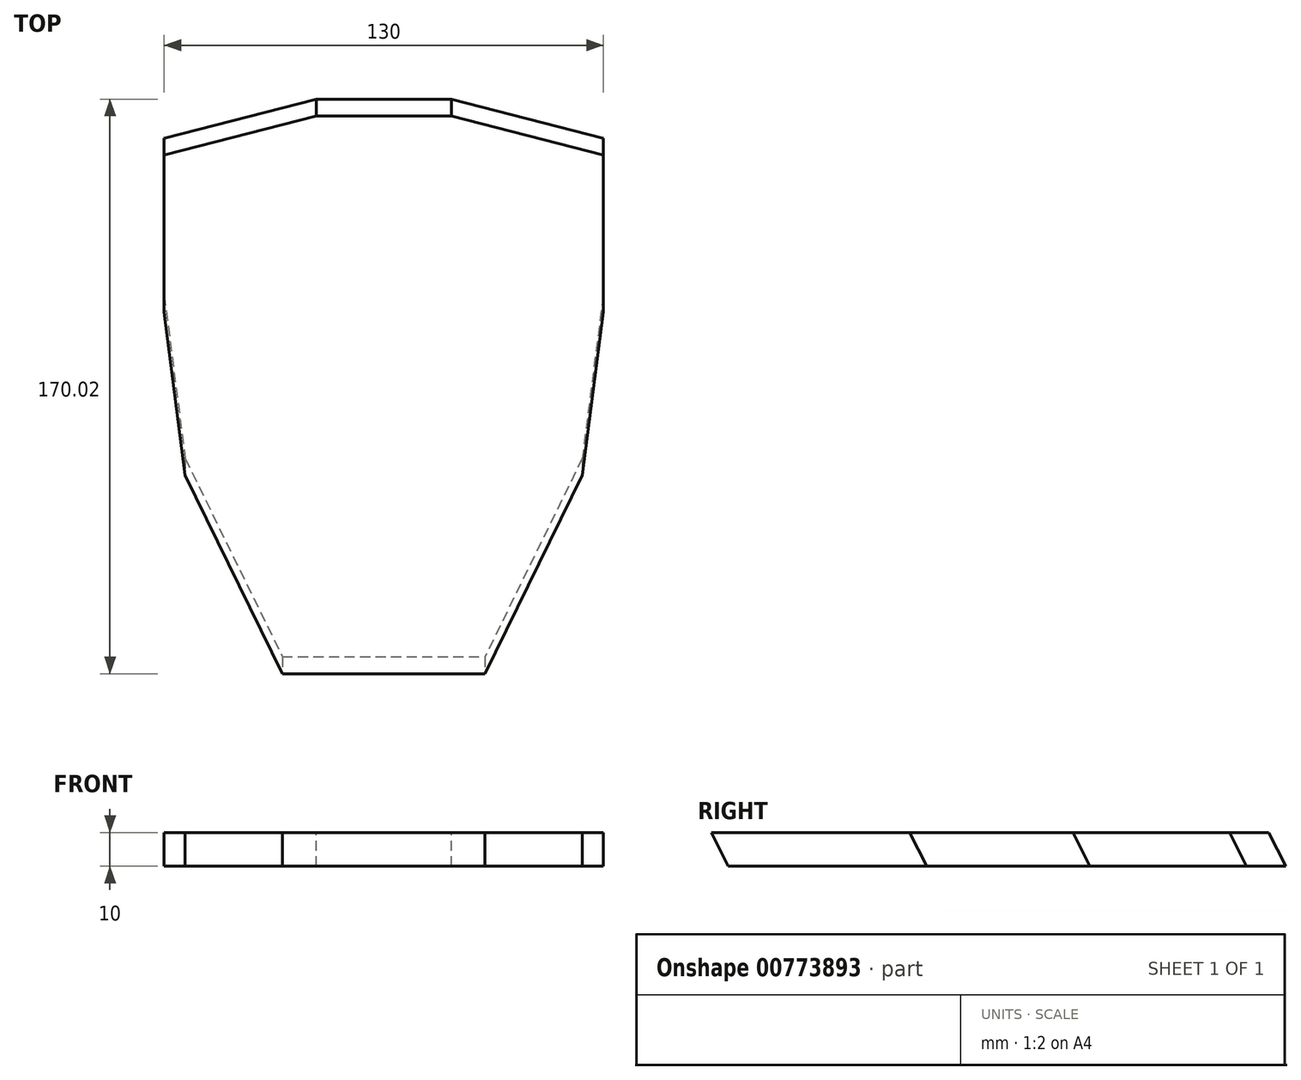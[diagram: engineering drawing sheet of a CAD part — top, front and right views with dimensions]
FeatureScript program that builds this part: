
annotation { "Feature Type Name" : "Feature", "Feature Type Description" : "" }
export const myFeature = defineFeature(function(context is Context, id is Id, definition is map)
    precondition{}
    {
        {
            var Q0;
            Q0=qCreatedBy(makeId("Top.planeOp"),FACE);
            var sketch = newSketch(context, id + "F0", { "sketchPlane" : qUnion([Q0])});
            skLineSegment(sketch, "E0", {"start": v(20, 40.27) * mm, "end": v(-20, 40.27) * mm});
            skPoint(sketch, "E1.orphan", {"position": v(0, 40.27) * mm});
            skLineSegment(sketch, "E2", {"start": v(-20, 40.27) * mm, "end": v(-65, 28.68) * mm});
            skLineSegment(sketch, "E3.MirrorCS", {"start": v(20, 40.27) * mm, "end": v(65, 28.68) * mm});
            skLineSegment(sketch, "E4", {"start": v(-65, 28.68) * mm, "end": v(-65, -17.7) * mm});
            skLineSegment(sketch, "E5", {"start": v(-65, -17.7) * mm, "end": v(-58.77, -66.04) * mm});
            skLineSegment(sketch, "E6", {"start": v(-58.77, -66.04) * mm, "end": v(-30, -124.75) * mm});
            skLineSegment(sketch, "E7", {"start": v(-30, -124.75) * mm, "end": v(30, -124.75) * mm});
            skLineSegment(sketch, "E8.MirrorCS", {"start": v(58.77, -66.04) * mm, "end": v(30, -124.75) * mm});
            skLineSegment(sketch, "E9.MirrorCS", {"start": v(65, -17.7) * mm, "end": v(58.77, -66.04) * mm});
            skLineSegment(sketch, "E10.MirrorCS", {"start": v(65, 28.68) * mm, "end": v(65, -17.7) * mm});
            skSolve(sketch);
        }
        {
            var Q0;
            Q0=qCreatedBy(makeId("Top.planeOp"),FACE);
            cPlane(context, id + "F1", {"entities" : qUnion([Q0]), "cplaneType" : CPlaneType.OFFSET, "offset" : 10 * mm, "width" : 150 * mm, "height" : 150 * mm});
        }
        {
            var Q0;
            Q0=qCreatedBy(id+"F1.planeOp",FACE);
            var sketch = newSketch(context, id + "F2", { "sketchPlane" : qUnion([Q0])});
            skLineSegment(sketch, "E11.0.0", {"start": v(65, -22.7) * mm, "end": v(65, 23.68) * mm});
            skLineSegment(sketch, "E11.0.1", {"start": v(65, 23.68) * mm, "end": v(20, 35.27) * mm});
            skLineSegment(sketch, "E11.0.2", {"start": v(20, 35.27) * mm, "end": v(-20, 35.27) * mm});
            skLineSegment(sketch, "E11.0.3", {"start": v(-20, 35.27) * mm, "end": v(-65, 23.68) * mm});
            skLineSegment(sketch, "E11.0.4", {"start": v(-65, 23.68) * mm, "end": v(-65, -22.7) * mm});
            skLineSegment(sketch, "E11.0.5", {"start": v(-65, -22.7) * mm, "end": v(-58.77, -71.04) * mm});
            skLineSegment(sketch, "E11.0.6", {"start": v(-58.77, -71.04) * mm, "end": v(-30, -129.75) * mm});
            skLineSegment(sketch, "E11.0.7", {"start": v(-30, -129.75) * mm, "end": v(30, -129.75) * mm});
            skLineSegment(sketch, "E11.0.8", {"start": v(30, -129.75) * mm, "end": v(58.77, -71.04) * mm});
            skLineSegment(sketch, "E11.0.9", {"start": v(58.77, -71.04) * mm, "end": v(65, -22.7) * mm});
            skSolve(sketch);
        }
        {
            var Q0;
            Q0=makeQuery(id+"F0.imprint","IMPRINT",FACE,{"disambiguationData":[TD([[makeQuery(id+"F0.imprint","IMPRINT",EDGE,{"derivedFrom":sQuery(id+"F0.wireOp",EDGE,"E0")}),1.0]])]});
            var Q1;
            Q1=makeQuery(id+"F2.imprint","IMPRINT",FACE,{"disambiguationData":[TD([[makeQuery(id+"F2.imprint","IMPRINT",EDGE,{"derivedFrom":sQuery(id+"F2.wireOp",EDGE,"E11.0.0")}),1.0]])]});
            loft(context, id + "F3", {"sheetProfilesArray" : [{ "sheetProfileEntities" : qUnion([Q0]) }, { "sheetProfileEntities" : qUnion([Q1]) }]});
        }
        {
            var Q0;
            Q0=makeQuery(id+"F3.opLoft","MID_CAP_EDGE",EDGE,{"disambiguationData":[OSD([sQuery(id+"F2.wireOp",EDGE,"E11.0.6"),sQuery(id+"F2.wireOp",EDGE,"E11.0.7"),sQuery(id+"F2.wireOp",EDGE,"E11.0.8")])],"capPos":1.0});
            cPlane(context, id + "F4", {"entities" : qUnion([Q0]), "cplaneType" : CPlaneType.LINE_ANGLE, "offset" : 25 * mm, "angle" : 30 * degree, "oppositeDirection" : true, "width" : 150 * mm, "height" : 150 * mm});
        }
        {
            var Q0;
            Q0=qCreatedBy(id+"F4.planeOp",FACE);
            var sketch = newSketch(context, id + "F5", { "sketchPlane" : qUnion([Q0])});
            skPoint(sketch, "E12.0", {"position": v(30, -56.21) * mm});
            skPoint(sketch, "E13.0", {"position": v(-30, -56.21) * mm});
            skLineSegment(sketch, "E14", {"start": v(30, -56.21) * mm, "end": v(30, -6.21) * mm});
            skLineSegment(sketch, "E15", {"start": v(-30, -56.21) * mm, "end": v(-30, -6.21) * mm});
            skLineSegment(sketch, "E16", {"start": v(-30, -6.21) * mm, "end": v(30, -6.21) * mm});
            skSolve(sketch);
        }
        {
            var Q0;
            Q0=qCreatedBy(makeId("Right.planeOp"),FACE);
            var Q1;
            Q1=makeQuery(id+"F3.opLoft","MID_CAP_EDGE",EDGE,{"disambiguationData":[OSD([sQuery(id+"F2.wireOp",EDGE,"E11.0.7"),sQuery(id+"F2.wireOp",EDGE,"E11.0.8"),sQuery(id+"F2.wireOp",EDGE,"E11.0.9")])],"capPos":1.0});
            cPlane(context, id + "F6", {"entities" : qUnion([Q0, Q1]), "cplaneType" : CPlaneType.LINE_ANGLE, "offset" : 25 * mm, "angle" : 30 * degree, "oppositeDirection" : true, "width" : 150 * mm, "height" : 150 * mm});
        }
        {
            var Q0;
            Q0=qCreatedBy(id+"F6.planeOp",FACE);
            var sketch = newSketch(context, id + "F7", { "sketchPlane" : qUnion([Q0])});
            skLineSegment(sketch, "E17", {"start": v(108.27, -7.81) * mm, "end": v(81.23, 37.04) * mm});
            skLineSegment(sketch, "E18", {"start": v(81.23, 37.04) * mm, "end": v(44.77, 37.04) * mm});
            skPoint(sketch, "E19.0", {"position": v(44.77, -23.38) * mm});
            skLineSegment(sketch, "E20", {"start": v(44.77, -23.38) * mm, "end": v(44.77, 37.04) * mm});
            skPoint(sketch, "E21.0", {"position": v(108.27, -7.81) * mm});
            skLineSegment(sketch, "E22", {"start": v(108.27, -7.81) * mm, "end": v(44.77, -23.38) * mm});
            skSolve(sketch);
        }
        {
            var Q0;
            Q0=makeQuery(id+"F3.opLoft","MID_CAP_EDGE",EDGE,{"disambiguationData":[OSD([sQuery(id+"F2.wireOp",EDGE,"E11.0.5"),sQuery(id+"F2.wireOp",EDGE,"E11.0.6"),sQuery(id+"F2.wireOp",EDGE,"E11.0.7")])],"capPos":1.0});
            cPlane(context, id + "F8", {"entities" : qUnion([Q0]), "cplaneType" : CPlaneType.LINE_ANGLE, "offset" : 25 * mm, "angle" : 60 * degree, "width" : 150 * mm, "height" : 150 * mm});
        }
        {
            var Q0;
            Q0=qCreatedBy(id+"F8.planeOp",FACE);
            var sketch = newSketch(context, id + "F9", { "sketchPlane" : qUnion([Q0])});
            skLineSegment(sketch, "E23", {"start": v(-81.23, 37.04) * mm, "end": v(-108.27, -7.81) * mm});
            skLineSegment(sketch, "E24.0", {"start": v(-95.47, 61.06) * mm, "end": v(-81.23, 37.04) * mm, "construction": true});
            skLineSegment(sketch, "E25", {"start": v(-81.23, 37.04) * mm, "end": v(-44.77, 37.04) * mm});
            skPoint(sketch, "E26.0", {"position": v(-44.77, -23.38) * mm});
            skLineSegment(sketch, "E27", {"start": v(-44.77, -23.38) * mm, "end": v(-44.77, 37.04) * mm});
            skPoint(sketch, "E28.0", {"position": v(-108.27, -7.81) * mm});
            skPoint(sketch, "E29.orphan", {"position": v(-76.23, 28.6) * mm});
            skLineSegment(sketch, "E30", {"start": v(-44.77, -23.38) * mm, "end": v(-108.27, -7.81) * mm});
            skSolve(sketch);
        }
        {
            var Q0;
            Q0=qCreatedBy(id+"F4.planeOp",FACE);
            var sketch = newSketch(context, id + "F10", { "sketchPlane" : qUnion([Q0])});
            skPoint(sketch, "E31.0", {"position": v(30, -56.21) * mm});
            skPoint(sketch, "E32.0", {"position": v(14.41, -6.21) * mm});
            skPoint(sketch, "E33.0", {"position": v(-14.41, -6.21) * mm});
            skPoint(sketch, "E34.0", {"position": v(-30, -56.21) * mm});
            skLineSegment(sketch, "E35", {"start": v(30, -56.21) * mm, "end": v(14.41, -6.21) * mm});
            skLineSegment(sketch, "E36", {"start": v(-14.41, -6.21) * mm, "end": v(-30, -56.21) * mm});
            skLineSegment(sketch, "E37", {"start": v(14.41, -6.21) * mm, "end": v(-14.41, -6.21) * mm});
            skLineSegment(sketch, "E38", {"start": v(30, -56.21) * mm, "end": v(-30, -56.21) * mm});
            skSolve(sketch);
        }
        {
            var Q0;
            Q0=sQuery(id+"F9.wireOp",EDGE,"E27");
            var Q1;
            Q1=makeQuery(id+"F3.opLoft","MID_CAP_EDGE",EDGE,{"disambiguationData":[OSD([sQuery(id+"F2.wireOp",EDGE,"E11.0.4"),sQuery(id+"F2.wireOp",EDGE,"E11.0.5"),sQuery(id+"F2.wireOp",EDGE,"E11.0.6")])],"capPos":1.0});
            cPlane(context, id + "F11", {"entities" : qUnion([Q0, Q1]), "cplaneType" : CPlaneType.LINE_ANGLE, "offset" : 25 * mm, "angle" : 0 * degree, "width" : 150 * mm, "height" : 150 * mm});
        }
        {
            var Q0;
            Q0=qCreatedBy(id+"F11.planeOp",FACE);
            var sketch = newSketch(context, id + "F12", { "sketchPlane" : qUnion([Q0])});
            skPoint(sketch, "E39.0", {"position": v(-64.72, 37.04) * mm});
            skPoint(sketch, "E40.0", {"position": v(-16.1, -26.74) * mm});
            skPoint(sketch, "E41.0", {"position": v(-64.72, -23.38) * mm});
            skLineSegment(sketch, "E42", {"start": v(-16.1, -26.74) * mm, "end": v(-16.1, 37.04) * mm});
            skLineSegment(sketch, "E43", {"start": v(-16.1, 37.04) * mm, "end": v(-64.72, 37.04) * mm});
            skLineSegment(sketch, "E44", {"start": v(-64.72, 37.04) * mm, "end": v(-64.72, -23.38) * mm});
            skLineSegment(sketch, "E45", {"start": v(-16.1, -26.74) * mm, "end": v(-64.72, -23.38) * mm});
            skSolve(sketch);
        }
        {
            var Q0;
            Q0=sQuery(id+"F7.wireOp",EDGE,"E20");
            var Q1;
            Q1=makeQuery(id+"F3.opLoft","MID_CAP_EDGE",EDGE,{"disambiguationData":[OSD([sQuery(id+"F2.wireOp",EDGE,"E11.0.0"),sQuery(id+"F2.wireOp",EDGE,"E11.0.8"),sQuery(id+"F2.wireOp",EDGE,"E11.0.9")])],"capPos":1.0});
            cPlane(context, id + "F13", {"entities" : qUnion([Q0, Q1]), "cplaneType" : CPlaneType.LINE_ANGLE, "offset" : 25 * mm, "angle" : 0 * degree, "width" : 150 * mm, "height" : 150 * mm});
        }
        {
            var Q0;
            Q0=qCreatedBy(id+"F13.planeOp",FACE);
            var sketch = newSketch(context, id + "F14", { "sketchPlane" : qUnion([Q0])});
            skPoint(sketch, "E46.0", {"position": v(64.72, 37.04) * mm});
            skPoint(sketch, "E47.0", {"position": v(64.72, -23.38) * mm});
            skPoint(sketch, "E48.0", {"position": v(16.1, -26.74) * mm});
            skLineSegment(sketch, "E49", {"start": v(64.72, 37.04) * mm, "end": v(16.1, 37.04) * mm});
            skLineSegment(sketch, "E50", {"start": v(16.1, 37.04) * mm, "end": v(16.1, -26.74) * mm});
            skLineSegment(sketch, "E51", {"start": v(64.72, 37.04) * mm, "end": v(64.72, -23.38) * mm});
            skLineSegment(sketch, "E52", {"start": v(64.72, -23.38) * mm, "end": v(16.1, -26.74) * mm});
            skSolve(sketch);
        }
        {
            var Q0;
            Q0=sQuery(id+"F14.wireOp",EDGE,"E50");
            var Q1;
            Q1=makeQuery(id+"F3.opLoft","MID_CAP_EDGE",EDGE,{"disambiguationData":[OSD([sQuery(id+"F2.wireOp",EDGE,"E11.0.0"),sQuery(id+"F2.wireOp",EDGE,"E11.0.1"),sQuery(id+"F2.wireOp",EDGE,"E11.0.9")])],"capPos":1.0});
            cPlane(context, id + "F15", {"entities" : qUnion([Q0, Q1]), "cplaneType" : CPlaneType.LINE_ANGLE, "offset" : 25 * mm, "angle" : 0 * degree, "width" : 150 * mm, "height" : 150 * mm});
        }
        {
            var Q0;
            Q0=qCreatedBy(id+"F15.planeOp",FACE);
            var sketch = newSketch(context, id + "F16", { "sketchPlane" : qUnion([Q0])});
            skPoint(sketch, "E53.0", {"position": v(-22.7, 37.04) * mm});
            skPoint(sketch, "E54.0", {"position": v(-22.7, -26.74) * mm});
            skPoint(sketch, "E55.0", {"position": v(23.68, -26.74) * mm});
            skLineSegment(sketch, "E56", {"start": v(23.68, 37.04) * mm, "end": v(23.68, -26.74) * mm});
            skLineSegment(sketch, "E57", {"start": v(-22.7, 37.04) * mm, "end": v(23.68, 37.04) * mm});
            skSolve(sketch);
        }
        {
            var Q0;
            Q0=sQuery(id+"F12.wireOp",EDGE,"E42");
            var Q1;
            Q1=makeQuery(id+"F3.opLoft","MID_CAP_EDGE",EDGE,{"disambiguationData":[OSD([sQuery(id+"F2.wireOp",EDGE,"E11.0.3"),sQuery(id+"F2.wireOp",EDGE,"E11.0.4"),sQuery(id+"F2.wireOp",EDGE,"E11.0.5")])],"capPos":1.0});
            cPlane(context, id + "F17", {"entities" : qUnion([Q0, Q1]), "cplaneType" : CPlaneType.LINE_ANGLE, "offset" : 25 * mm, "angle" : 0 * degree, "width" : 150 * mm, "height" : 150 * mm});
        }
        {
            var Q0;
            Q0=qCreatedBy(id+"F17.planeOp",FACE);
            var sketch = newSketch(context, id + "F18", { "sketchPlane" : qUnion([Q0])});
            skPoint(sketch, "E58.0", {"position": v(-22.7, 37.04) * mm});
            skPoint(sketch, "E59.0", {"position": v(23.68, -26.74) * mm});
            skLineSegment(sketch, "E60", {"start": v(-22.7, 37.04) * mm, "end": v(23.68, 37.04) * mm});
            skLineSegment(sketch, "E61", {"start": v(23.68, 37.04) * mm, "end": v(23.68, -26.74) * mm});
            skSolve(sketch);
        }
        {
            var Q0;
            Q0=makeQuery(id+"F3.opLoft","MID_CAP_EDGE",EDGE,{"disambiguationData":[OSD([sQuery(id+"F2.wireOp",EDGE,"E11.0.0"),sQuery(id+"F2.wireOp",EDGE,"E11.0.1"),sQuery(id+"F2.wireOp",EDGE,"E11.0.2")])],"capPos":1.0});
            cPlane(context, id + "F19", {"entities" : qUnion([Q0]), "cplaneType" : CPlaneType.LINE_ANGLE, "offset" : 25 * mm, "angle" : 30 * degree, "oppositeDirection" : true, "width" : 150 * mm, "height" : 150 * mm});
        }
        {
            var Q0;
            Q0=qCreatedBy(id+"F19.planeOp",FACE);
            var sketch = newSketch(context, id + "F20", { "sketchPlane" : qUnion([Q0])});
            skLineSegment(sketch, "E62", {"start": v(22.63, 54.37) * mm, "end": v(57.96, -3.54) * mm});
            skLineSegment(sketch, "E63", {"start": v(57.96, -3.54) * mm, "end": v(11.88, -9.47) * mm});
            skLineSegment(sketch, "E64", {"start": v(22.63, 54.37) * mm, "end": v(11.88, 52.99) * mm});
            skLineSegment(sketch, "E65", {"start": v(11.88, 52.99) * mm, "end": v(11.88, -9.47) * mm});
            skSolve(sketch);
        }
        {
            var Q0;
            Q0=makeQuery(id+"F3.opLoft","MID_CAP_EDGE",EDGE,{"disambiguationData":[OSD([sQuery(id+"F2.wireOp",EDGE,"E11.0.1"),sQuery(id+"F2.wireOp",EDGE,"E11.0.2"),sQuery(id+"F2.wireOp",EDGE,"E11.0.3")])],"capPos":1.0});
            var Q1;
            Q1=sQuery(id+"F20.wireOp",EDGE,"E65");
            cPlane(context, id + "F21", {"entities" : qUnion([Q0, Q1]), "cplaneType" : CPlaneType.LINE_ANGLE, "offset" : 25 * mm, "angle" : 0 * degree, "width" : 150 * mm, "height" : 150 * mm});
        }
        {
            var Q0;
            Q0=qCreatedBy(id+"F21.planeOp",FACE);
            var sketch = newSketch(context, id + "F22", { "sketchPlane" : qUnion([Q0])});
            skPoint(sketch, "E66.0", {"position": v(20, 52.99) * mm});
            skPoint(sketch, "E67.0", {"position": v(-20, 52.99) * mm});
            skLineSegment(sketch, "E68", {"start": v(20, 52.99) * mm, "end": v(-20, 52.99) * mm});
            skPoint(sketch, "E69.0", {"position": v(20, -9.47) * mm});
            skPoint(sketch, "E70.0", {"position": v(-20, -9.47) * mm});
            skLineSegment(sketch, "E71", {"start": v(-20, 52.99) * mm, "end": v(-20, -9.47) * mm});
            skLineSegment(sketch, "E72", {"start": v(20, -9.47) * mm, "end": v(20, 52.99) * mm});
            skLineSegment(sketch, "E73", {"start": v(20, -9.47) * mm, "end": v(-20, -9.47) * mm});
            skSolve(sketch);
        }
        {
            var Q0;
            Q0=qCreatedBy(id+"F17.planeOp",FACE);
            var sketch = newSketch(context, id + "F23", { "sketchPlane" : qUnion([Q0])});
            skPoint(sketch, "E74.0", {"position": v(0.55, 37.06) * mm});
            skPoint(sketch, "E75.0", {"position": v(-22.7, 37.04) * mm});
            skPoint(sketch, "E76.0", {"position": v(-22.7, -26.74) * mm});
            skPoint(sketch, "E77.0", {"position": v(23.68, -26.74) * mm});
            skLineSegment(sketch, "E78", {"start": v(23.68, -26.74) * mm, "end": v(0.55, 37.06) * mm});
            skLineSegment(sketch, "E79", {"start": v(-22.7, 37.04) * mm, "end": v(-22.7, -26.74) * mm});
            skLineSegment(sketch, "E80", {"start": v(0.55, 37.06) * mm, "end": v(-22.7, 37.04) * mm});
            skLineSegment(sketch, "E81", {"start": v(23.68, -26.74) * mm, "end": v(-22.7, -26.74) * mm});
            skSolve(sketch);
        }
        {
            var Q0;
            Q0=qCreatedBy(id+"F15.planeOp",FACE);
            var sketch = newSketch(context, id + "F24", { "sketchPlane" : qUnion([Q0])});
            skPoint(sketch, "E82.0", {"position": v(-22.7, 37.04) * mm});
            skPoint(sketch, "E83.0", {"position": v(0.49, 37.04) * mm});
            skPoint(sketch, "E84.0", {"position": v(23.68, -26.74) * mm});
            skPoint(sketch, "E85.0", {"position": v(-22.7, -26.74) * mm});
            skLineSegment(sketch, "E86", {"start": v(-22.7, -26.74) * mm, "end": v(-22.7, 37.04) * mm});
            skLineSegment(sketch, "E87", {"start": v(-22.7, 37.04) * mm, "end": v(0.49, 37.04) * mm});
            skLineSegment(sketch, "E88", {"start": v(0.49, 37.04) * mm, "end": v(23.68, -26.74) * mm});
            skLineSegment(sketch, "E89", {"start": v(23.68, -26.74) * mm, "end": v(-22.7, -26.74) * mm});
            skSolve(sketch);
        }
        {
            var Q0;
            Q0=sQuery(id+"F23.wireOp",EDGE,"E80");
            var Q1;
            Q1=sQuery(id+"FC3jcg2qtJbTTqg_1.1.F20.wireOp",EDGE,"E64");
            cPlane(context, id + "F25", {"entities" : qUnion([Q0, Q1]), "cplaneType" : CPlaneType.LINE_ANGLE, "offset" : 25 * mm, "angle" : 0 * degree, "width" : 150 * mm, "height" : 150 * mm});
        }
        {
            var Q0;
            Q0=qCreatedBy(id+"F25.planeOp",FACE);
            var sketch = newSketch(context, id + "F26", { "sketchPlane" : qUnion([Q0])});
            skPoint(sketch, "E90.0", {"position": v(-30.52, -22.65) * mm});
            skPoint(sketch, "E91.0", {"position": v(-20.01, 3.35) * mm});
            skLineSegment(sketch, "E92", {"start": v(-30.52, -22.65) * mm, "end": v(-20.01, 3.35) * mm});
            skPoint(sketch, "E93.0", {"position": v(-30.5, 0.61) * mm});
            skLineSegment(sketch, "E94", {"start": v(-30.52, -22.65) * mm, "end": v(-30.5, 0.61) * mm});
            skLineSegment(sketch, "E95", {"start": v(-30.5, 0.61) * mm, "end": v(-20.01, 3.35) * mm});
            skSolve(sketch);
        }
        {
            var Q0;
            Q0=sQuery(id+"F24.wireOp",EDGE,"E87");
            var Q1;
            Q1=sQuery(id+"F20.wireOp",EDGE,"E64");
            cPlane(context, id + "F27", {"entities" : qUnion([Q0, Q1]), "cplaneType" : CPlaneType.LINE_ANGLE, "offset" : 25 * mm, "angle" : 0 * degree, "width" : 150 * mm, "height" : 150 * mm});
        }
        {
            var Q0;
            Q0=qCreatedBy(id+"F27.planeOp",FACE);
            var sketch = newSketch(context, id + "F28", { "sketchPlane" : qUnion([Q0])});
            skPoint(sketch, "E96.0", {"position": v(30.5, -22.7) * mm});
            skPoint(sketch, "E97.0", {"position": v(20, 3.29) * mm});
            skLineSegment(sketch, "E98", {"start": v(30.5, -22.7) * mm, "end": v(20, 3.29) * mm});
            skPoint(sketch, "E99.0", {"position": v(30.52, 0.55) * mm});
            skLineSegment(sketch, "E100", {"start": v(20, 3.29) * mm, "end": v(30.52, 0.55) * mm});
            skLineSegment(sketch, "E101", {"start": v(30.52, 0.55) * mm, "end": v(30.5, -22.7) * mm});
            skSolve(sketch);
        }
        {
            var Q0;
            Q0=sQuery(id+"F14.wireOp",EDGE,"E49");
            var Q1;
            Q1=sQuery(id+"F12.wireOp",EDGE,"E43");
            cPlane(context, id + "F29", {"entities" : qUnion([Q0, Q1]), "cplaneType" : CPlaneType.LINE_ANGLE, "offset" : 25 * mm, "angle" : 0 * degree, "width" : 150 * mm, "height" : 150 * mm});
        }
        {
            var Q0;
            Q0=sQuery(id+"F9.wireOp",EDGE,"E25");
            var Q1;
            Q1=sQuery(id+"F7.wireOp",EDGE,"E18");
            cPlane(context, id + "F30", {"entities" : qUnion([Q0, Q1]), "cplaneType" : CPlaneType.LINE_ANGLE, "offset" : 25 * mm, "angle" : 0 * degree, "width" : 150 * mm, "height" : 150 * mm});
        }
        {
            var Q0;
            Q0=sQuery(id+"F26.wireOp",EDGE,"E92");
            var Q1;
            Q1=sQuery(id+"F28.wireOp",EDGE,"E98");
            var Q2;
            Q2 = qBodyType(qCreatedBy(id + "F32" ,EDGE), BodyType.WIRE);
            cPlane(context, id + "F31", {"entities" : qUnion([Q0, Q1, Q2]), "cplaneType" : CPlaneType.LINE_ANGLE, "offset" : 25 * mm, "angle" : 0 * degree, "width" : 150 * mm, "height" : 150 * mm});
        }
        {
            var Q0;
            Q0=qCreatedBy(id+"F31.planeOp",FACE);
            var sketch = newSketch(context, id + "F32", { "sketchPlane" : qUnion([Q0])});
            skPoint(sketch, "E102.0", {"position": v(30.57, -22.68) * mm});
            skPoint(sketch, "E103.0", {"position": v(20.06, 3.31) * mm});
            skPoint(sketch, "E104.0", {"position": v(-19.94, 3.31) * mm});
            skPoint(sketch, "E105.0", {"position": v(-30.44, -22.68) * mm});
            skLineSegment(sketch, "E106", {"start": v(30.57, -22.68) * mm, "end": v(-30.44, -22.68) * mm});
            skLineSegment(sketch, "E107", {"start": v(-19.94, 3.31) * mm, "end": v(20.06, 3.31) * mm});
            skLineSegment(sketch, "E108", {"start": v(30.57, -22.68) * mm, "end": v(20.06, 3.31) * mm});
            skLineSegment(sketch, "E109", {"start": v(-19.94, 3.31) * mm, "end": v(-30.44, -22.68) * mm});
            skSolve(sketch);
        }
        {
            var Q0;
            Q0=makeQuery(id+"F3.opLoft","SWEPT_BODY",BODY,{"disambiguationData":[OSD([makeQuery(id+"F0.imprint","IMPRINT",FACE,{"disambiguationData":[TD([[makeQuery(id+"F0.imprint","IMPRINT",EDGE,{"derivedFrom":sQuery(id+"F0.wireOp",EDGE,"E0")}),1.0]])]}),makeQuery(id+"F2.imprint","IMPRINT",FACE,{"disambiguationData":[TD([[makeQuery(id+"F2.imprint","IMPRINT",EDGE,{"derivedFrom":sQuery(id+"F2.wireOp",EDGE,"E11.0.0")}),1.0]])]})])]});
            var Q1;
            Q1=qCreatedBy(makeId("Right.planeOp"),FACE);
            mirror(context, id + "F33", {"operationType" : NewBodyOperationType.ADD, "entities" : qUnion([Q0]), "mirrorPlane" : qUnion([Q1])});
        }
    });
